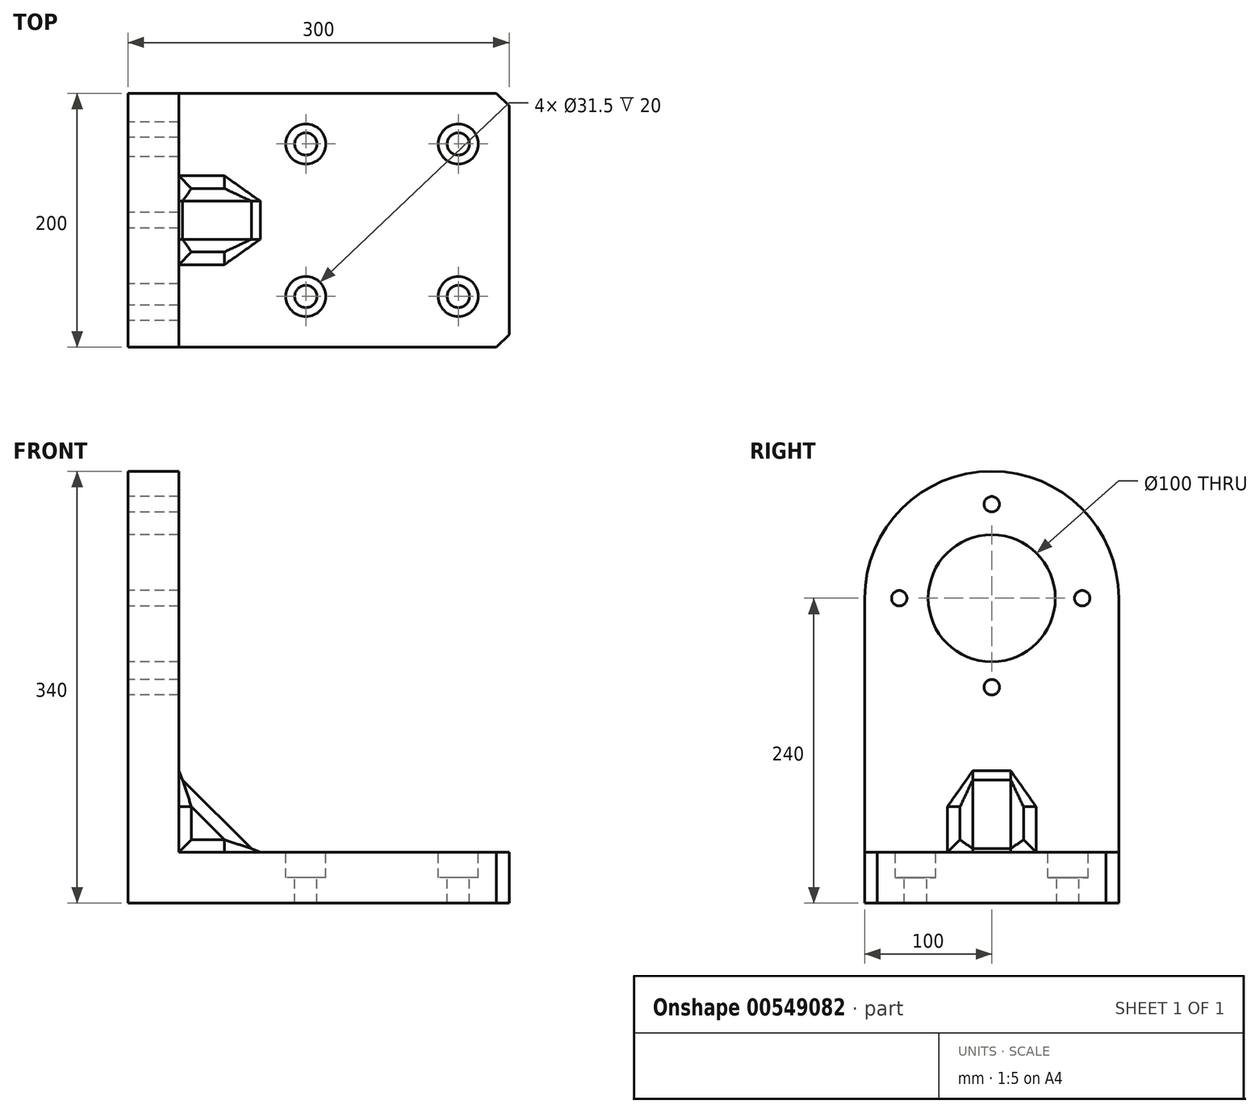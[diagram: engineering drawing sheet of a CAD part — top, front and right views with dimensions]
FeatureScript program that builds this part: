
annotation { "Feature Type Name" : "Feature", "Feature Type Description" : "" }
export const myFeature = defineFeature(function(context is Context, id is Id, definition is map)
    precondition{}
    {
        {
            var Q0;
            Q0=qCreatedBy(makeId("Top.planeOp"),FACE);
            var sketch = newSketch(context, id + "F0", { "sketchPlane" : qUnion([Q0])});
            skLineSegment(sketch, "E0.bottom", {"start": v(290, -100) * mm, "end": v(0, -100) * mm});
            skLineSegment(sketch, "E0.top", {"start": v(290, 100) * mm, "end": v(0, 100) * mm});
            skLineSegment(sketch, "E0.left", {"start": v(300, -90) * mm, "end": v(300, 90) * mm});
            skLineSegment(sketch, "E0.right", {"start": v(0, -100) * mm, "end": v(0, 100) * mm});
            skPoint(sketch, "E0.middle", {"position": v(150, 0) * mm});
            skLineSegment(sketch, "E1", {"start": v(290, -100) * mm, "end": v(300, -90) * mm});
            skLineSegment(sketch, "E2", {"start": v(290, 100) * mm, "end": v(300, 90) * mm});
            skPoint(sketch, "E3.orphan", {"position": v(300, 100) * mm});
            skPoint(sketch, "E4.orphan", {"position": v(300, -100) * mm});
            skCircle(sketch, "E5", {"center": v(260, 60) * mm, "radius": 15.75 * mm});
            skLineSegment(sketch, "E6", {"start": v(260, 60) * mm, "end": v(260, -60) * mm, "construction": true});
            skCircle(sketch, "E7", {"center": v(260, -60) * mm, "radius": 15.75 * mm});
            skCircle(sketch, "E8", {"center": v(140, 60) * mm, "radius": 15.75 * mm});
            skCircle(sketch, "E9", {"center": v(140, -60) * mm, "radius": 15.75 * mm});
            skLineSegment(sketch, "E10", {"start": v(140, 60) * mm, "end": v(260, 60) * mm, "construction": true});
            skLineSegment(sketch, "E11", {"start": v(140, -60) * mm, "end": v(140, 60) * mm, "construction": true});
            skLineSegment(sketch, "E12", {"start": v(140, -60) * mm, "end": v(260, -60) * mm, "construction": true});
            skSolve(sketch);
        }
        {
            var Q0;
            Q0=qCreatedBy(makeId("Right.planeOp"),FACE);
            var sketch = newSketch(context, id + "F1", { "sketchPlane" : qUnion([Q0])});
            skLineSegment(sketch, "E13.left", {"start": v(-100, 0) * mm, "end": v(-100, 200) * mm});
            skLineSegment(sketch, "E13.right", {"start": v(100, 0) * mm, "end": v(100, 200) * mm});
            skPoint(sketch, "E13.middle", {"position": v(0, 0) * mm});
            skPoint(sketch, "E14.orphan", {"position": v(100, -200) * mm});
            skPoint(sketch, "E15.orphan", {"position": v(-100, -200) * mm});
            skLineSegment(sketch, "E16", {"start": v(100, 0) * mm, "end": v(-100, 0) * mm});
            skArc(sketch, "E17", {"start": v(100, 200) * mm, "mid": v(0, 300) * mm, "end": v(-100, 200) * mm});
            skLineSegment(sketch, "E18", {"start": v(0, 300) * mm, "end": v(0, 0) * mm, "construction": true});
            skLineSegment(sketch, "E19", {"start": v(100, 40) * mm, "end": v(-100, 40) * mm});
            skCircle(sketch, "E20", {"center": v(0, 200) * mm, "radius": 50 * mm});
            skPoint(sketch, "E21", {"position": v(0, 273.98) * mm});
            skPoint(sketch, "E22", {"position": v(71.2, 200) * mm});
            skPoint(sketch, "E23", {"position": v(-72.8, 200) * mm});
            skPoint(sketch, "E24", {"position": v(0, 129.98) * mm});
            skSolve(sketch);
        }
        {
            var Q0;
            Q0 = qSketchRegion(id + "F1", true);
            extrude(context, id + "F2", {"entities" : qUnion([Q0]), "depth" : 40 * mm, "offsetDistance" : 25 * mm});
        }
        {
            var Q0;
            Q0=sQuery(id+"F1.wireOp",VERTEX,"E21");
            var Q1;
            Q1=sQuery(id+"F1.wireOp",VERTEX,"E23");
            var Q2;
            Q2=sQuery(id+"F1.wireOp",VERTEX,"E24");
            var Q3;
            Q3=sQuery(id+"F1.wireOp",VERTEX,"E22");
            var Q4;
            Q4=makeQuery(id+"F2.opExtrude","SWEPT_BODY",BODY,{"disambiguationData":[OSD([sQuery(id+"F1.wireOp",EDGE,"E13.left"),sQuery(id+"F1.wireOp",EDGE,"E13.right"),sQuery(id+"F1.wireOp",EDGE,"E16"),sQuery(id+"F1.wireOp",EDGE,"E17"),sQuery(id+"F1.wireOp",EDGE,"E20")])]});
            hole(context, id + "F3", {"style" : HoleStyle.SIMPLE, "endStyle" : HoleEndStyle.THROUGH, "oppositeDirection" : true, "standardTappedOrClearance" : lookupTablePath({ "standard" : "ISO", "engagement" : "75%", "pitch" : "2 mm", "size" : "M14", "type" : "Tapped" }), "standardBlindInLast" : lookupTablePath({ "standard" : "ISO", "engagement" : "75%", "pitch" : "2 mm", "size" : "M14", "type" : "Tapped" }), "holeDiameter" : 12.1 * mm, "showTappedDepth" : true, "isTappedThrough" : true, "tappedDepth" : 12 * mm, "tapClearance" : 3, "locations" : qUnion([Q0, Q1, Q2, Q3]), "scope" : qUnion([Q4]), "majorDiameter" : 14 * mm});
        }
        {
            var Q0;
            Q0=makeQuery(id+"F0.imprint","IMPRINT",FACE,{"disambiguationData":[TD([[makeQuery(id+"F0.imprint","IMPRINT",EDGE,{"derivedFrom":sQuery(id+"F0.wireOp",EDGE,"E0.bottom")}),-1.0]])]});
            var Q1;
            Q1=makeQuery(id+"F0.imprint","IMPRINT",FACE,{"disambiguationData":[TD([[makeQuery(id+"F0.imprint","IMPRINT",EDGE,{"derivedFrom":sQuery(id+"F0.wireOp",EDGE,"E5")}),1.0]])]});
            var Q2;
            Q2=makeQuery(id+"F0.imprint","IMPRINT",FACE,{"disambiguationData":[TD([[makeQuery(id+"F0.imprint","IMPRINT",EDGE,{"derivedFrom":sQuery(id+"F0.wireOp",EDGE,"E8")}),1.0]])]});
            var Q3;
            Q3=makeQuery(id+"F0.imprint","IMPRINT",FACE,{"disambiguationData":[TD([[makeQuery(id+"F0.imprint","IMPRINT",EDGE,{"derivedFrom":sQuery(id+"F0.wireOp",EDGE,"E9")}),1.0]])]});
            var Q4;
            Q4=makeQuery(id+"F0.imprint","IMPRINT",FACE,{"disambiguationData":[TD([[makeQuery(id+"F0.imprint","IMPRINT",EDGE,{"derivedFrom":sQuery(id+"F0.wireOp",EDGE,"E7")}),1.0]])]});
            extrude(context, id + "F4", {"entities" : qUnion([Q0, Q1, Q2, Q3, Q4]), "operationType" : NewBodyOperationType.ADD, "oppositeDirection" : true, "depth" : 40 * mm, "offsetDistance" : 25 * mm});
        }
        {
            var Q0;
            Q0=qCreatedBy(makeId("Front.planeOp"),FACE);
            var sketch = newSketch(context, id + "F5", { "sketchPlane" : qUnion([Q0])});
            skPoint(sketch, "E25.orphan", {"position": v(40, 200) * mm});
            skPoint(sketch, "E26.orphan", {"position": v(290, -40) * mm});
            skLineSegment(sketch, "E27.0", {"start": v(290, 0) * mm, "end": v(0, 0) * mm});
            skLineSegment(sketch, "E28.0", {"start": v(40, 0) * mm, "end": v(40, 200) * mm});
            skLineSegment(sketch, "E29", {"start": v(100, 0) * mm, "end": v(40, 60) * mm});
            skSolve(sketch);
        }
        {
            var Q0;
            Q0 = qSketchRegion(id + "F5", true);
            extrude(context, id + "F6", {"entities" : qUnion([Q0]), "operationType" : NewBodyOperationType.ADD, "endBound" : BoundingType.SYMMETRIC, "depth" : 50 * mm, "offsetDistance" : 25 * mm});
        }
        {
            var Q0;
            Q0=makeQuery(id+"F2.opExtrude","CAP_EDGE",EDGE,{"disambiguationData":[OSD([sQuery(id+"F1.wireOp",EDGE,"E16")])],"isStart":true});
            var Q1;
            Q1=makeQuery(id+"F6.opExtrude","SWEPT_FACE",FACE,{"disambiguationData":[OSD([sQuery(id+"F5.wireOp",EDGE,"E29")])]});
            chamfer(context, id + "F7", {"entities" : qUnion([Q0, Q1]), "width" : 10 * mm, "tangentPropagation" : true});
        }
        {
            var Q0;
            Q0=sQuery(id+"F0.wireOp",VERTEX,"E9.center");
            var Q1;
            Q1=sQuery(id+"F0.wireOp",VERTEX,"E7.center");
            var Q2;
            Q2=sQuery(id+"F0.wireOp",VERTEX,"E5.center");
            var Q3;
            Q3=sQuery(id+"F0.wireOp",VERTEX,"E8.center");
            var Q4;
            Q4=makeQuery(id+"F2.opExtrude","SWEPT_BODY",BODY,{"disambiguationData":[OSD([sQuery(id+"F1.wireOp",EDGE,"E13.left"),sQuery(id+"F1.wireOp",EDGE,"E13.right"),sQuery(id+"F1.wireOp",EDGE,"E16"),sQuery(id+"F1.wireOp",EDGE,"E17"),sQuery(id+"F1.wireOp",EDGE,"E20")])]});
            hole(context, id + "F8", {"style" : HoleStyle.C_BORE, "endStyle" : HoleEndStyle.THROUGH, "holeDiameter" : 17.5 * mm, "cBoreDiameter" : 31.5 * mm, "cBoreDepth" : 20 * mm, "isTappedThrough" : true, "tappedDepth" : 12 * mm, "tapClearance" : 3, "locations" : qUnion([Q0, Q1, Q2, Q3]), "scope" : qUnion([Q4])});
        }
    });
